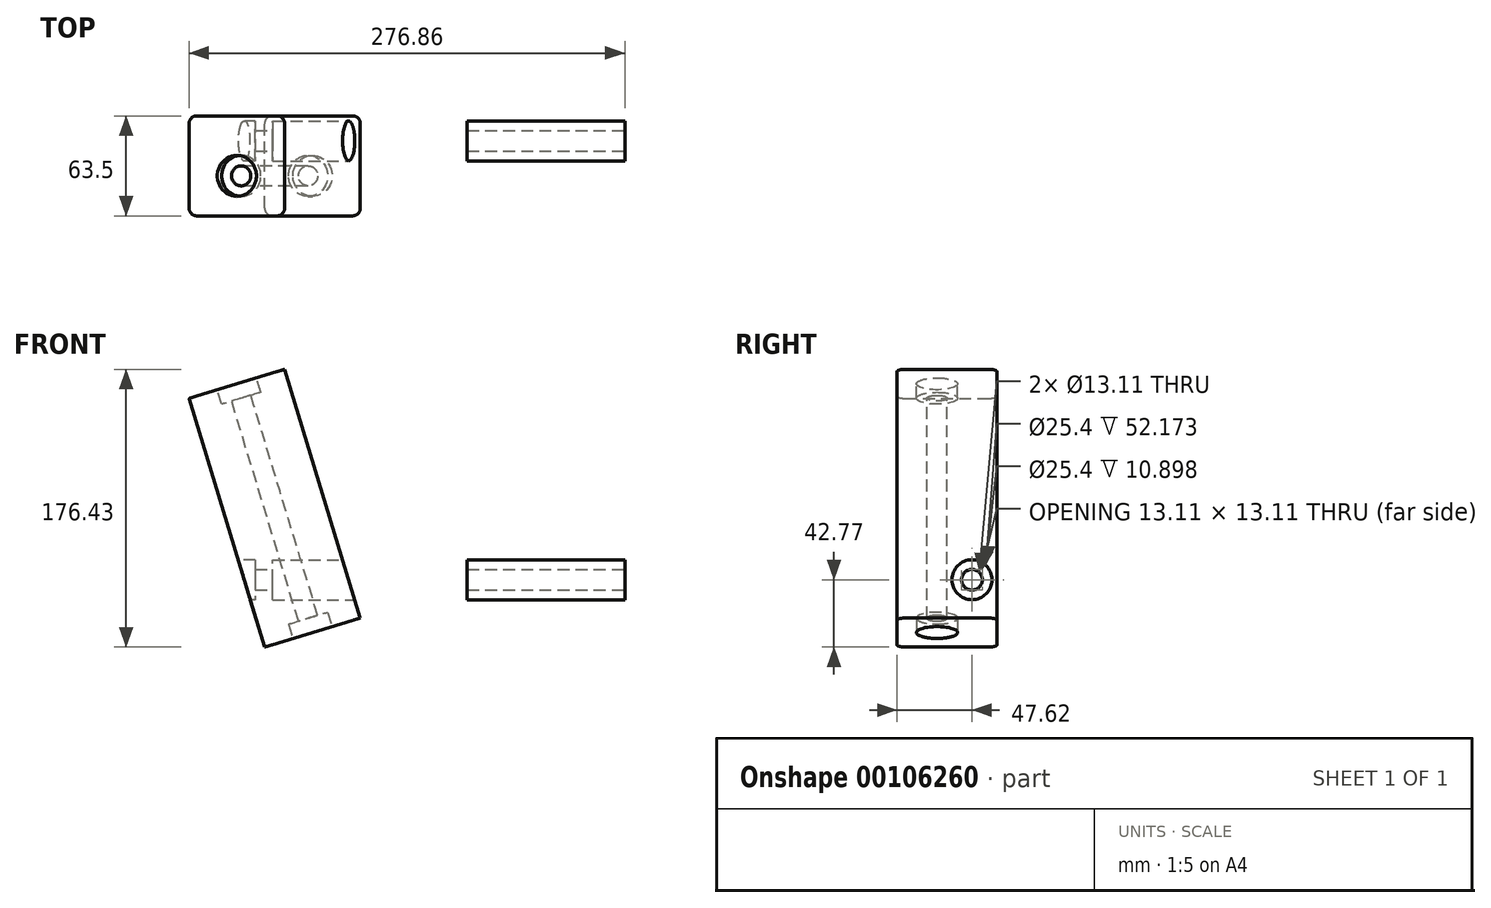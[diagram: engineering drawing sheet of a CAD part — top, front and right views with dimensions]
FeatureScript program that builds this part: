
annotation { "Feature Type Name" : "Feature", "Feature Type Description" : "" }
export const myFeature = defineFeature(function(context is Context, id is Id, definition is map)
    precondition{}
    {
        {
            var Q0;
            Q0=qCreatedBy(makeId("Front.planeOp"),FACE);
            var sketch = newSketch(context, id + "F0", { "sketchPlane" : qUnion([Q0])});
            skLineSegment(sketch, "E0.bottom", {"start": v(-36.8, -12.7) * mm, "end": v(63.5, -12.7) * mm});
            skLineSegment(sketch, "E0.top", {"start": v(-36.8, 12.7) * mm, "end": v(63.5, 12.7) * mm});
            skLineSegment(sketch, "E0.left", {"start": v(-36.8, -12.7) * mm, "end": v(-36.8, 12.7) * mm});
            skLineSegment(sketch, "E0.right", {"start": v(63.5, -12.7) * mm, "end": v(63.5, 12.7) * mm});
            skLineSegment(sketch, "E1", {"start": v(-36.8, 12.7) * mm, "end": v(0, 22.56) * mm, "construction": true});
            skLineSegment(sketch, "E2", {"start": v(-36.8, 0) * mm, "end": v(63.5, 0) * mm});
            skSolve(sketch);
        }
        {
            var Q0;
            {var subQ0=sQuery(id+"F0.wireOp",EDGE,"E0.top");Q0=makeQuery(id+"F0.imprint","IMPRINT",FACE,{"disambiguationData":[TD([[makeQuery(id+"F0.imprint","IMPRINT",EDGE,{"derivedFrom":subQ0}),-1.0]])]});}
            var Q1;
            Q1=sQuery(id+"F0.wireOp",EDGE,"E2");
            revolve(context, id + "F1", {"entities" : qUnion([Q0]), "axis" : qUnion([Q1]), "revolveType" : RevolveType.FULL});
        }
        {
            var Q0;
            Q0=makeQuery(id+"F1.opRevolve","SWEPT_FACE",FACE,{"disambiguationData":[OSD([sQuery(id+"F0.wireOp",EDGE,"E0.right")])]});
            var sketch = newSketch(context, id + "F2", { "sketchPlane" : qUnion([Q0])});
            skPoint(sketch, "E3", {"position": v(0, 0) * mm});
            skSolve(sketch);
        }
        {
            var Q0;
            Q0=sQuery(id+"F2.wireOp",VERTEX,"E3");
            var Q1;
            Q1=makeQuery(id+"F1.opRevolve","SWEPT_BODY",BODY,{"disambiguationData":[OSD([sQuery(id+"F0.wireOp",EDGE,"E0.top"),sQuery(id+"F0.wireOp",EDGE,"E0.left"),sQuery(id+"F0.wireOp",EDGE,"E0.right"),sQuery(id+"F0.wireOp",EDGE,"E2")])]});
            hole(context, id + "F3", {"style" : HoleStyle.SIMPLE, "endStyle" : HoleEndStyle.THROUGH, "standardTappedOrClearance" : lookupTablePath({ "standard" : "ANSI", "fit" : "Close", "size" : "1/2", "type" : "Clearance" }), "standardBlindInLast" : lookupTablePath({ "fit" : "Close", "standard" : "ANSI", "size" : "1/2", "type" : "Clearance" }), "holeDiameter" : 13.1 * mm, "locations" : qUnion([Q0]), "scope" : qUnion([Q1]), "isTappedThrough" : true});
        }
        {
            var Q0;
            Q0=qCreatedBy(makeId("Front.planeOp"),FACE);
            var sketch = newSketch(context, id + "F4", { "sketchPlane" : qUnion([Q0])});
            skLineSegment(sketch, "E4", {"start": v(-165.33, -42.77) * mm, "end": v(-104.58, -24.3) * mm});
            skLineSegment(sketch, "E5", {"start": v(-104.58, -24.3) * mm, "end": v(-152.6, 133.66) * mm});
            skLineSegment(sketch, "E6", {"start": v(-152.6, 133.66) * mm, "end": v(-213.36, 115.19) * mm});
            skLineSegment(sketch, "E7", {"start": v(-213.36, 115.19) * mm, "end": v(-165.33, -42.77) * mm});
            skLineSegment(sketch, "E8", {"start": v(-76.46, 0) * mm, "end": v(-202.09, 0) * mm, "construction": true});
            skPoint(sketch, "E9", {"position": v(-111.97, 0) * mm});
            skPoint(sketch, "E10", {"position": v(-178.34, 0) * mm});
            skSolve(sketch);
        }
        {
            var Q0;
            Q0 = qSketchRegion(id + "F4", true);
            extrude(context, id + "F5", {"entities" : qUnion([Q0]), "depth" : 47.62 * mm, "hasSecondDirection" : true, "secondDirectionOppositeDirection" : true, "secondDirectionDepth" : 15.88 * mm});
        }
        {
            var Q0;
            Q0=qCreatedBy(makeId("Right.planeOp"),FACE);
            var sketch = newSketch(context, id + "F6", { "sketchPlane" : qUnion([Q0])});
            skPoint(sketch, "E11", {"position": v(0, 0) * mm});
            skSolve(sketch);
        }
        {
            var Q0;
            Q0=sQuery(id+"F6.wireOp",VERTEX,"E11");
            var Q1;
            Q1=makeQuery(id+"F5.opExtrude","SWEPT_BODY",BODY,{"disambiguationData":[OSD([sQuery(id+"F4.wireOp",EDGE,"E4"),sQuery(id+"F4.wireOp",EDGE,"E5"),sQuery(id+"F4.wireOp",EDGE,"E6"),sQuery(id+"F4.wireOp",EDGE,"E7")])]});
            hole(context, id + "F7", {"style" : HoleStyle.SIMPLE, "endStyle" : HoleEndStyle.THROUGH, "standardTappedOrClearance" : lookupTablePath({ "standard" : "ANSI", "fit" : "Close", "size" : "1/2", "type" : "Clearance" }), "standardBlindInLast" : lookupTablePath({ "fit" : "Close", "standard" : "ANSI", "size" : "1/2", "type" : "Clearance" }), "holeDiameter" : 13.1 * mm, "locations" : qUnion([Q0]), "scope" : qUnion([Q1]), "isTappedThrough" : true});
        }
        {
            var Q0;
            Q0=qCreatedBy(makeId("Right.planeOp"),FACE);
            var sketch = newSketch(context, id + "F8", { "sketchPlane" : qUnion([Q0])});
            skPoint(sketch, "E12", {"position": v(0, 0) * mm});
            skSolve(sketch);
        }
        {
            var Q0;
            Q0=sQuery(id+"F8.wireOp",VERTEX,"E12");
            var Q1;
            Q1=makeQuery(id+"F5.opExtrude","SWEPT_BODY",BODY,{"disambiguationData":[OSD([sQuery(id+"F4.wireOp",EDGE,"E4"),sQuery(id+"F4.wireOp",EDGE,"E5"),sQuery(id+"F4.wireOp",EDGE,"E6"),sQuery(id+"F4.wireOp",EDGE,"E7")])]});
            hole(context, id + "F9", {"style" : HoleStyle.C_BORE, "endStyle" : HoleEndStyle.BLIND, "holeDiameter" : 12.7 * mm, "cBoreDiameter" : 25.4 * mm, "cBoreDepth" : 44.45 * mm, "holeDepth" : 44.45 * mm, "locations" : qUnion([Q0]), "scope" : qUnion([Q1])});
        }
        {
            var Q0;
            Q0=qCreatedBy(makeId("Right.planeOp"),FACE);
            cPlane(context, id + "F10", {"entities" : qUnion([Q0]), "cplaneType" : CPlaneType.OFFSET, "offset" : 203.2 * mm, "oppositeDirection" : true, "width" : 152.4 * mm, "height" : 152.4 * mm});
        }
        {
            var Q0;
            Q0=qCreatedBy(id+"F10.planeOp",FACE);
            var sketch = newSketch(context, id + "F11", { "sketchPlane" : qUnion([Q0])});
            skPoint(sketch, "E13", {"position": v(0, 0) * mm});
            skSolve(sketch);
        }
        {
            var Q0;
            Q0=sQuery(id+"F11.wireOp",VERTEX,"E13");
            var Q1;
            Q1=makeQuery(id+"F5.opExtrude","SWEPT_BODY",BODY,{"disambiguationData":[OSD([sQuery(id+"F4.wireOp",EDGE,"E4"),sQuery(id+"F4.wireOp",EDGE,"E5"),sQuery(id+"F4.wireOp",EDGE,"E6"),sQuery(id+"F4.wireOp",EDGE,"E7")])]});
            hole(context, id + "F12", {"style" : HoleStyle.C_BORE, "endStyle" : HoleEndStyle.BLIND, "oppositeDirection" : true, "holeDiameter" : 12.7 * mm, "cBoreDiameter" : 25.4 * mm, "cBoreDepth" : 3.17 * mm, "holeDepth" : 12.7 * mm, "locations" : qUnion([Q0]), "scope" : qUnion([Q1])});
        }
        {
            var Q0;
            Q0=makeQuery(id+"F5.opExtrude","CAP_EDGE",EDGE,{"disambiguationData":[OSD([sQuery(id+"F4.wireOp",EDGE,"E5")])],"isStart":false});
            var Q1;
            Q1=makeQuery(id+"F5.opExtrude","CAP_EDGE",EDGE,{"disambiguationData":[OSD([sQuery(id+"F4.wireOp",EDGE,"E5")])],"isStart":true});
            var Q2;
            Q2=makeQuery(id+"F5.opExtrude","CAP_EDGE",EDGE,{"disambiguationData":[OSD([sQuery(id+"F4.wireOp",EDGE,"E7")])],"isStart":false});
            var Q3;
            Q3=makeQuery(id+"F5.opExtrude","CAP_EDGE",EDGE,{"disambiguationData":[OSD([sQuery(id+"F4.wireOp",EDGE,"E7")])],"isStart":true});
            fillet(context, id + "F13", {"entities" : qUnion([Q0, Q1, Q2, Q3]), "radius" : 5.08 * mm, "tangentPropagation" : true, "allowEdgeOverflow" : false});
        }
        {
            var Q0;
            Q0=makeQuery(id+"F5.opExtrude","SWEPT_FACE",FACE,{"disambiguationData":[OSD([sQuery(id+"F4.wireOp",EDGE,"E6")])]});
            var sketch = newSketch(context, id + "F14", { "sketchPlane" : qUnion([Q0])});
            skPoint(sketch, "E14", {"position": v(-138.88, -22.22) * mm});
            skSolve(sketch);
        }
        {
            var Q0;
            Q0=sQuery(id+"F14.wireOp",VERTEX,"E14");
            var Q1;
            Q1=makeQuery(id+"F5.opExtrude","SWEPT_BODY",BODY,{"disambiguationData":[OSD([sQuery(id+"F4.wireOp",EDGE,"E4"),sQuery(id+"F4.wireOp",EDGE,"E5"),sQuery(id+"F4.wireOp",EDGE,"E6"),sQuery(id+"F4.wireOp",EDGE,"E7")])]});
            hole(context, id + "F15", {"style" : HoleStyle.SIMPLE, "endStyle" : HoleEndStyle.THROUGH, "holeDiameter" : 12.7 * mm, "locations" : qUnion([Q0]), "scope" : qUnion([Q1]), "isTappedThrough" : true});
        }
        {
            var Q0;
            Q0=makeQuery(id+"F5.opExtrude","SWEPT_FACE",FACE,{"disambiguationData":[OSD([sQuery(id+"F4.wireOp",EDGE,"E6")])]});
            var sketch = newSketch(context, id + "F16", { "sketchPlane" : qUnion([Q0])});
            skPoint(sketch, "E15", {"position": v(-138.88, -22.22) * mm});
            skSolve(sketch);
        }
        {
            var Q0;
            Q0=sQuery(id+"F16.wireOp",VERTEX,"E15");
            var Q1;
            Q1=makeQuery(id+"F5.opExtrude","SWEPT_BODY",BODY,{"disambiguationData":[OSD([sQuery(id+"F4.wireOp",EDGE,"E4"),sQuery(id+"F4.wireOp",EDGE,"E5"),sQuery(id+"F4.wireOp",EDGE,"E6"),sQuery(id+"F4.wireOp",EDGE,"E7")])]});
            hole(context, id + "F17", {"style" : HoleStyle.C_BORE, "endStyle" : HoleEndStyle.BLIND, "holeDiameter" : 12.7 * mm, "cBoreDiameter" : 26.03 * mm, "cBoreDepth" : 9.52 * mm, "holeDepth" : 12.7 * mm, "locations" : qUnion([Q0]), "scope" : qUnion([Q1])});
        }
        {
            var Q0;
            Q0=makeQuery(id+"F5.opExtrude","SWEPT_FACE",FACE,{"disambiguationData":[OSD([sQuery(id+"F4.wireOp",EDGE,"E4")])]});
            var sketch = newSketch(context, id + "F18", { "sketchPlane" : qUnion([Q0])});
            skPoint(sketch, "E16", {"position": v(-138.88, 22.22) * mm});
            skSolve(sketch);
        }
        {
            var Q0;
            Q0=sQuery(id+"F18.wireOp",VERTEX,"E16");
            var Q1;
            Q1=makeQuery(id+"F5.opExtrude","SWEPT_BODY",BODY,{"disambiguationData":[OSD([sQuery(id+"F4.wireOp",EDGE,"E4"),sQuery(id+"F4.wireOp",EDGE,"E5"),sQuery(id+"F4.wireOp",EDGE,"E6"),sQuery(id+"F4.wireOp",EDGE,"E7")])]});
            hole(context, id + "F19", {"style" : HoleStyle.C_BORE, "endStyle" : HoleEndStyle.BLIND, "holeDiameter" : 12.7 * mm, "cBoreDiameter" : 26.03 * mm, "cBoreDepth" : 9.52 * mm, "holeDepth" : 12.7 * mm, "locations" : qUnion([Q0]), "scope" : qUnion([Q1])});
        }
    });
